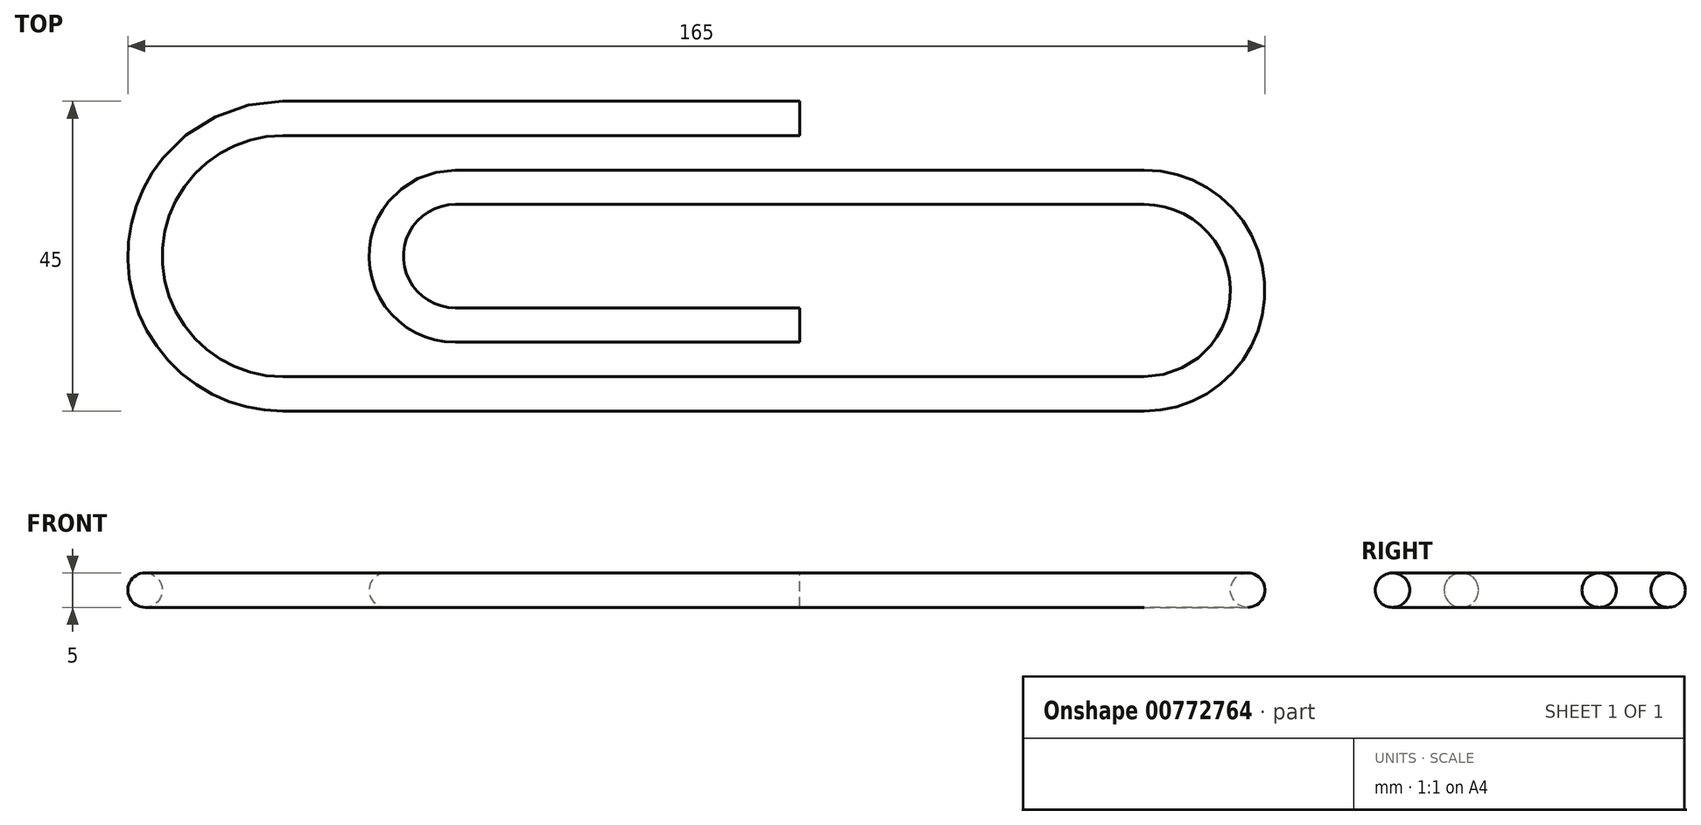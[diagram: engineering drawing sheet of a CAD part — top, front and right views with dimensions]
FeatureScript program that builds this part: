
annotation { "Feature Type Name" : "Feature", "Feature Type Description" : "" }
export const myFeature = defineFeature(function(context is Context, id is Id, definition is map)
    precondition{}
    {
        {
            var Q0;
            Q0=qCreatedBy(makeId("Top.planeOp"),FACE);
            var sketch = newSketch(context, id + "F0", { "sketchPlane" : qUnion([Q0])});
            skLineSegment(sketch, "E0", {"start": v(0, 0) * mm, "end": v(-75, 0) * mm});
            skLineSegment(sketch, "E1", {"start": v(-75, -40) * mm, "end": v(50, -40) * mm});
            skLineSegment(sketch, "E2", {"start": v(50, -10) * mm, "end": v(-50, -10) * mm});
            skLineSegment(sketch, "E3", {"start": v(-50, -30) * mm, "end": v(0, -30) * mm});
            skArc(sketch, "E4", {"start": v(-75, 0) * mm, "mid": v(-95, -20) * mm, "end": v(-75, -40) * mm});
            skArc(sketch, "E5", {"start": v(-50, -10) * mm, "mid": v(-60, -20) * mm, "end": v(-50, -30) * mm});
            skArc(sketch, "E6", {"start": v(50, -10) * mm, "mid": v(65, -25) * mm, "end": v(50, -40) * mm});
            skSolve(sketch);
        }
        {
            var Q0;
            Q0=qCreatedBy(makeId("Right.planeOp"),FACE);
            var sketch = newSketch(context, id + "F1", { "sketchPlane" : qUnion([Q0])});
            skCircle(sketch, "E7", {"center": v(0, 0) * mm, "radius": 2.5 * mm});
            skSolve(sketch);
        }
        {
            var Q0;
            Q0 = qSketchRegion(id + "F1", true);
            var Q1;
            Q1 = qConstructionFilter(qBodyType(qCreatedBy(id + "F0" ,EDGE), BodyType.WIRE), ConstructionObject.NO);
            sweep(context, id + "F2", {"profiles" : qUnion([Q0]), "path" : qUnion([Q1])});
        }
    });
